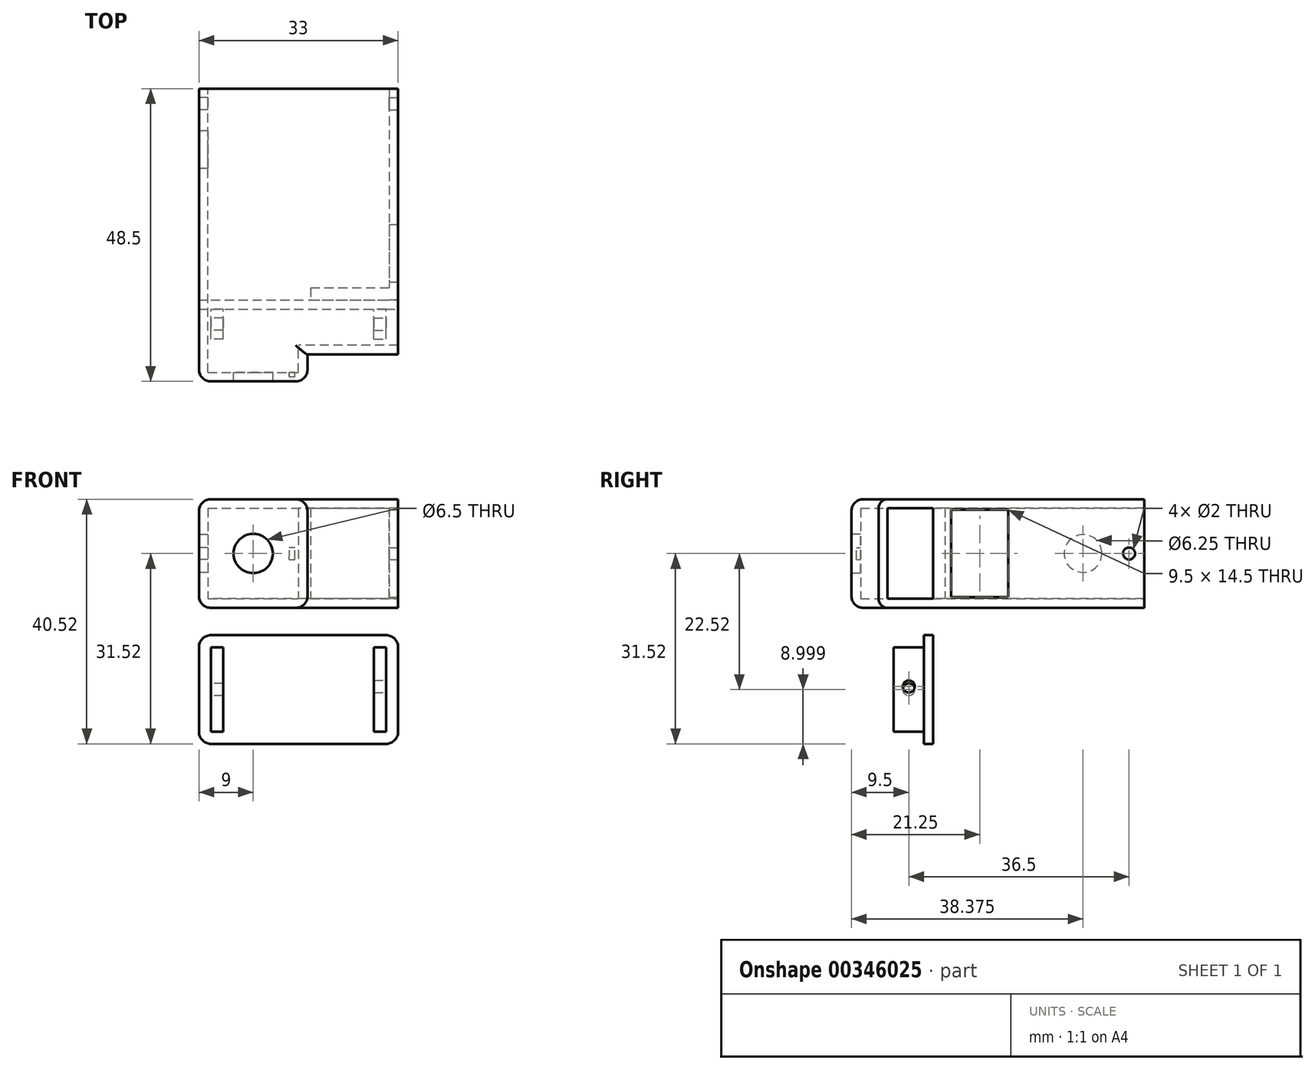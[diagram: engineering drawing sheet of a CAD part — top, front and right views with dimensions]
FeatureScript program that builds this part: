
annotation { "Feature Type Name" : "Feature", "Feature Type Description" : "" }
export const myFeature = defineFeature(function(context is Context, id is Id, definition is map)
    precondition{}
    {
        {
            var Q0;
            Q0=qCreatedBy(makeId("Front.planeOp"),FACE);
            var sketch = newSketch(context, id + "F0", { "sketchPlane" : qUnion([Q0])});
            skCircle(sketch, "E0", {"center": v(7.5, 7) * mm, "radius": 4.5 * mm});
            skCircle(sketch, "E1", {"center": v(7.5, 7) * mm, "radius": 3.25 * mm});
            skCircle(sketch, "E2", {"center": v(7.5, 7) * mm, "radius": 1.5 * mm});
            skLineSegment(sketch, "E3", {"start": v(36.83, 0) * mm, "end": v(36.83, 9.5) * mm, "construction": true});
            skLineSegment(sketch, "E4", {"start": v(36.83, 9.5) * mm, "end": v(49.83, 9.5) * mm, "construction": true});
            skLineSegment(sketch, "E5", {"start": v(49.83, 9.5) * mm, "end": v(49.83, 0) * mm, "construction": true});
            skLineSegment(sketch, "E6", {"start": v(49.83, 0) * mm, "end": v(36.83, 0) * mm, "construction": true});
            skLineSegment(sketch, "E7.0", {"start": v(14, 7) * mm, "end": v(1, 7) * mm, "construction": true});
            skLineSegment(sketch, "E8", {"start": v(14, 7) * mm, "end": v(33.97, 7) * mm, "construction": true});
            skLineSegment(sketch, "E9.0", {"start": v(14, -2) * mm, "end": v(33.97, -2) * mm, "construction": true});
            skLineSegment(sketch, "E10.0", {"start": v(14, -2) * mm, "end": v(0, -2) * mm, "construction": true});
            skLineSegment(sketch, "E11.0", {"start": v(7.5, 16) * mm, "end": v(7.5, -2) * mm, "construction": true});
            skLineSegment(sketch, "E12.0", {"start": v(16.5, 16) * mm, "end": v(16.5, -2) * mm});
            skLineSegment(sketch, "E13", {"start": v(0, 14.5) * mm, "end": v(0, -0.5) * mm});
            skLineSegment(sketch, "E14", {"start": v(-1.5, 16) * mm, "end": v(-1.5, -2) * mm});
            skLineSegment(sketch, "E15", {"start": v(-1.5, -2) * mm, "end": v(16.5, -2) * mm});
            skLineSegment(sketch, "E16", {"start": v(15, 14.5) * mm, "end": v(15, -0.5) * mm});
            skLineSegment(sketch, "E17", {"start": v(0, -0.5) * mm, "end": v(32.99, -0.5) * mm, "construction": true});
            skLineSegment(sketch, "E18", {"start": v(0, -0.5) * mm, "end": v(15, -0.5) * mm});
            skLineSegment(sketch, "E19", {"start": v(0, 14.5) * mm, "end": v(33.86, 14.5) * mm, "construction": true});
            skLineSegment(sketch, "E20", {"start": v(-1.5, 16) * mm, "end": v(36.08, 16) * mm, "construction": true});
            skLineSegment(sketch, "E21", {"start": v(-1.5, 16) * mm, "end": v(16.5, 16) * mm});
            skLineSegment(sketch, "E22", {"start": v(0, 14.5) * mm, "end": v(15, 14.5) * mm});
            skLineSegment(sketch, "E23", {"start": v(16.5, 14.5) * mm, "end": v(31.5, 14.5) * mm});
            skLineSegment(sketch, "E24", {"start": v(31.5, 14.5) * mm, "end": v(31.5, -0.5) * mm});
            skLineSegment(sketch, "E25", {"start": v(31.5, -0.5) * mm, "end": v(16.5, -0.5) * mm});
            skLineSegment(sketch, "E26", {"start": v(16.5, 16) * mm, "end": v(34.5, 16) * mm});
            skLineSegment(sketch, "E27", {"start": v(34.5, -2) * mm, "end": v(16.5, -2) * mm});
            skLineSegment(sketch, "E28.0", {"start": v(33, 16) * mm, "end": v(33, -2) * mm, "construction": true});
            skLineSegment(sketch, "E29", {"start": v(33, 16) * mm, "end": v(33, -2) * mm});
            skLineSegment(sketch, "E30", {"start": v(16.5, 14.5) * mm, "end": v(16.5, -0.5) * mm});
            skCircle(sketch, "E31", {"center": v(7.5, 7) * mm, "radius": 6 * mm});
            skSolve(sketch);
        }
        {
            var Q0;
            Q0=makeQuery(id+"F0.imprint","IMPRINT",FACE,{"disambiguationData":[TD([[makeQuery(id+"F0.imprint","IMPRINT",EDGE,{"derivedFrom":sQuery(id+"F0.wireOp",EDGE,"LJwKmjQE-U71p-W845-ssy2-OsRAPNaDEyHZ")}),1.0]])]});
            var Q1;
            Q1=makeQuery(id+"F0.imprint","IMPRINT",FACE,{"disambiguationData":[TD([[makeQuery(id+"F0.imprint","IMPRINT",EDGE,{"derivedFrom":sQuery(id+"F0.wireOp",EDGE,"E13")}),-1.0]])]});
            extrude(context, id + "F1", {"entities" : qUnion([Q0, Q1]), "depth" : 13.5 * mm});
        }
        {
            var Q0;
            Q0=makeQuery(id+"F0.imprint","IMPRINT",FACE,{"disambiguationData":[TD([[makeQuery(id+"F0.imprint","IMPRINT",EDGE,{"derivedFrom":sQuery(id+"F0.wireOp",EDGE,"E13")}),1.0]])]});
            extrude(context, id + "F2", {"entities" : qUnion([Q0]), "depth" : 13.5 * mm});
        }
        {
            var Q0;
            Q0=makeQuery(id+"F0.imprint","IMPRINT",FACE,{"disambiguationData":[TD([[makeQuery(id+"F0.imprint","IMPRINT",EDGE,{"derivedFrom":sQuery(id+"F0.wireOp",EDGE,"E13")}),1.0]])]});
            var Q1;
            Q1=makeQuery(id+"F0.imprint","IMPRINT",FACE,{"disambiguationData":[TD([[makeQuery(id+"F0.imprint","IMPRINT",EDGE,{"derivedFrom":sQuery(id+"F0.wireOp",EDGE,"E0")}),-1.0]])]});
            extrude(context, id + "F3", {"entities" : qUnion([Q0, Q1]), "operationType" : NewBodyOperationType.REMOVE, "depth" : 12 * mm});
        }
        {
            var Q0;
            Q0=makeQuery(id+"F1.opExtrude","SWEPT_FACE",FACE,{"disambiguationData":[OSD([sQuery(id+"F0.wireOp",EDGE,"E12.0"),sQuery(id+"F0.wireOp",EDGE,"E30")])]});
            var sketch = newSketch(context, id + "F4", { "sketchPlane" : qUnion([Q0])});
            skLineSegment(sketch, "E32.0", {"start": v(-13.5, 7) * mm, "end": v(0, 7) * mm, "construction": true});
            skLineSegment(sketch, "E33.0", {"start": v(-7.5, 16) * mm, "end": v(-7.5, -2) * mm, "construction": true});
            skLineSegment(sketch, "E34.0", {"start": v(-9, 16) * mm, "end": v(-9, -2) * mm, "construction": true});
            skLineSegment(sketch, "E35.0", {"start": v(-13.5, -0.5) * mm, "end": v(0, -0.5) * mm, "construction": true});
            skLineSegment(sketch, "E36.0", {"start": v(-13.5, 14.5) * mm, "end": v(0, 14.5) * mm, "construction": true});
            skLineSegment(sketch, "E37", {"start": v(0, -0.5) * mm, "end": v(-7.5, -0.5) * mm});
            skLineSegment(sketch, "E38", {"start": v(-7.5, -0.5) * mm, "end": v(-7.5, 14.5) * mm});
            skLineSegment(sketch, "E39", {"start": v(-7.5, 14.5) * mm, "end": v(0, 14.5) * mm});
            skLineSegment(sketch, "E40", {"start": v(0, -2) * mm, "end": v(-9, -2) * mm});
            skLineSegment(sketch, "E41", {"start": v(-9, 16) * mm, "end": v(0, 16) * mm});
            skLineSegment(sketch, "E42", {"start": v(-9, -2) * mm, "end": v(-9, 16) * mm});
            skSolve(sketch);
        }
        {
            var Q0;
            {var subQ2=sQuery(id+"F4.wireOp",EDGE,"E37");Q0=makeQuery(id+"F4.imprint","IMPRINT",FACE,{"disambiguationData":[TD([[makeQuery(id+"F4.imprint","IMPRINT",EDGE,{"derivedFrom":subQ2}),1.0]])]});}
            extrude(context, id + "F5", {"entities" : qUnion([Q0]), "operationType" : NewBodyOperationType.ADD, "depth" : 15 * mm});
        }
        {
            var Q0;
            {var subQ0=sQuery(id+"F4.wireOp",EDGE,"E37");var subQ1=sQuery(id+"F0.wireOp",EDGE,"E30");var subQ2=sQuery(id+"F0.wireOp",EDGE,"E12.0");Q0=makeQuery(id+"F5.boolean.opBoolean","SPLIT",FACE,{"disambiguationData":[TD([makeQuery(id+"F5.opExtrude","SWEPT_FACE",FACE,{"disambiguationData":[OSD([subQ0])]})])],"derivedFrom":makeQuery(id+"F1.opExtrude","SWEPT_FACE",FACE,{"disambiguationData":[OSD([subQ2,subQ1])]})});}
            extrude(context, id + "F6", {"entities" : qUnion([Q0]), "operationType" : NewBodyOperationType.REMOVE, "oppositeDirection" : true, "depth" : 1.5 * mm});
        }
        {
            var Q0;
            Q0=makeQuery(id+"F0.imprint","IMPRINT",FACE,{"disambiguationData":[TD([[makeQuery(id+"F0.imprint","IMPRINT",EDGE,{"derivedFrom":sQuery(id+"F0.wireOp",EDGE,"E13")}),-1.0]])]});
            var Q1;
            {var subQ0=sQuery(id+"F0.wireOp",EDGE,"E23");Q1=makeQuery(id+"F0.imprint","IMPRINT",FACE,{"disambiguationData":[TD([[makeQuery(id+"F0.imprint","IMPRINT",EDGE,{"derivedFrom":subQ0}),1.0]])]});}
            extrude(context, id + "F7", {"entities" : qUnion([Q0, Q1]), "operationType" : NewBodyOperationType.ADD, "oppositeDirection" : true, "depth" : 35 * mm});
        }
        {
            var Q0;
            Q0=makeQuery(id+"F7.opExtrude","CAP_FACE",FACE,{"disambiguationData":[OSD([sQuery(id+"F0.wireOp",EDGE,"E13"),sQuery(id+"F0.wireOp",EDGE,"E14"),sQuery(id+"F0.wireOp",EDGE,"E15"),sQuery(id+"F0.wireOp",EDGE,"E16"),sQuery(id+"F0.wireOp",EDGE,"E18"),sQuery(id+"F0.wireOp",EDGE,"E21"),sQuery(id+"F0.wireOp",EDGE,"E22"),sQuery(id+"F0.wireOp",EDGE,"E23"),sQuery(id+"F0.wireOp",EDGE,"E24"),sQuery(id+"F0.wireOp",EDGE,"E25"),sQuery(id+"F0.wireOp",EDGE,"E26"),sQuery(id+"F0.wireOp",EDGE,"E27"),sQuery(id+"F0.wireOp",EDGE,"E29"),sQuery(id+"F0.wireOp",EDGE,"E30")])],"isStart":false});
            var sketch = newSketch(context, id + "F8", { "sketchPlane" : qUnion([Q0])});
            skLineSegment(sketch, "E43", {"start": v(-16.5, 14.5) * mm, "end": v(-15, 14.5) * mm});
            skLineSegment(sketch, "E44", {"start": v(-15, 14.5) * mm, "end": v(-15, -0.5) * mm});
            skLineSegment(sketch, "E45", {"start": v(-15, -0.5) * mm, "end": v(-16.5, -0.5) * mm});
            skSolve(sketch);
        }
        {
            var Q0;
            Q0=makeQuery(id+"F8.imprint","IMPRINT",FACE,{"disambiguationData":[TD([[makeQuery(id+"F8.imprint","IMPRINT",EDGE,{"derivedFrom":sQuery(id+"F8.wireOp",EDGE,"E43")}),-1.0]])]});
            extrude(context, id + "F9", {"entities" : qUnion([Q0]), "operationType" : NewBodyOperationType.REMOVE, "oppositeDirection" : true, "depth" : 15 * mm});
        }
        {
            var Q0;
            Q0=makeQuery(id+"F7.opExtrude","SWEPT_FACE",FACE,{"disambiguationData":[OSD([sQuery(id+"F0.wireOp",EDGE,"E24")])]});
            var sketch = newSketch(context, id + "F10", { "sketchPlane" : qUnion([Q0])});
            skLineSegment(sketch, "E46.0", {"start": v(-15, 7) * mm, "end": v(0, 7) * mm, "construction": true});
            skLineSegment(sketch, "E47.0", {"start": v(-2, 14.5) * mm, "end": v(-2, -0.5) * mm, "construction": true});
            skLineSegment(sketch, "E48", {"start": v(-2, 14.5) * mm, "end": v(-2, -0.5) * mm});
            skSolve(sketch);
        }
        {
            var Q0;
            {var subQ0=sQuery(id+"F10.wireOp",EDGE,"E48");Q0=makeQuery(id+"F10.imprint","IMPRINT",FACE,{"disambiguationData":[TD([[makeQuery(id+"F10.imprint","IMPRINT",EDGE,{"derivedFrom":subQ0}),1.0]])]});}
            extrude(context, id + "F11", {"entities" : qUnion([Q0]), "operationType" : NewBodyOperationType.ADD, "depth" : 15 * mm});
        }
        {
            var Q0;
            Q0=makeQuery(id+"F7.opExtrude","CAP_FACE",FACE,{"disambiguationData":[OSD([sQuery(id+"F0.wireOp",EDGE,"E13"),sQuery(id+"F0.wireOp",EDGE,"E14"),sQuery(id+"F0.wireOp",EDGE,"E15"),sQuery(id+"F0.wireOp",EDGE,"E16"),sQuery(id+"F0.wireOp",EDGE,"E18"),sQuery(id+"F0.wireOp",EDGE,"E21"),sQuery(id+"F0.wireOp",EDGE,"E22"),sQuery(id+"F0.wireOp",EDGE,"E23"),sQuery(id+"F0.wireOp",EDGE,"E24"),sQuery(id+"F0.wireOp",EDGE,"E25"),sQuery(id+"F0.wireOp",EDGE,"E26"),sQuery(id+"F0.wireOp",EDGE,"E27"),sQuery(id+"F0.wireOp",EDGE,"E29"),sQuery(id+"F0.wireOp",EDGE,"E30")])],"isStart":false});
            var sketch = newSketch(context, id + "F12", { "sketchPlane" : qUnion([Q0])});
            skLineSegment(sketch, "E49", {"start": v(-31.5, -0.5) * mm, "end": v(-31.5, -2) * mm});
            skLineSegment(sketch, "E50", {"start": v(-31.5, 14.5) * mm, "end": v(-31.5, 16) * mm});
            skSolve(sketch);
        }
        {
            var Q0;
            {var subQ2=sQuery(id+"F12.wireOp",EDGE,"E49");Q0=makeQuery(id+"F12.imprint","IMPRINT",FACE,{"disambiguationData":[TD([[makeQuery(id+"F12.imprint","IMPRINT",EDGE,{"derivedFrom":subQ2}),-1.0]])]});}
            extrude(context, id + "F13", {"entities" : qUnion([Q0]), "operationType" : NewBodyOperationType.REMOVE, "oppositeDirection" : true, "depth" : 35 * mm});
        }
        {
            var Q0;
            Q0=makeQuery(id+"F11.opExtrude","SWEPT_FACE",FACE,{"disambiguationData":[OSD([sQuery(id+"F10.wireOp",EDGE,"E48")])]});
            var sketch = newSketch(context, id + "F14", { "sketchPlane" : qUnion([Q0])});
            skLineSegment(sketch, "E51.0", {"start": v(-30, 14.5) * mm, "end": v(-30, -0.5) * mm});
            skSolve(sketch);
        }
        {
            var Q0;
            {var subQ0=sQuery(id+"F14.wireOp",EDGE,"E51.0");Q0=makeQuery(id+"F14.imprint","IMPRINT",FACE,{"disambiguationData":[TD([[makeQuery(id+"F14.imprint","IMPRINT",EDGE,{"derivedFrom":subQ0}),-1.0]])]});}
            extrude(context, id + "F15", {"entities" : qUnion([Q0]), "operationType" : NewBodyOperationType.ADD, "depth" : 33 * mm});
        }
        {
            var Q0;
            Q0=qCreatedBy(makeId("Front.planeOp"),FACE);
            var sketch = newSketch(context, id + "F16", { "sketchPlane" : qUnion([Q0])});
            skLineSegment(sketch, "E52.0", {"start": v(-1.5, -6.52) * mm, "end": v(31.5, -6.52) * mm});
            skLineSegment(sketch, "E52.1", {"start": v(-1.5, -24.52) * mm, "end": v(-1.5, -6.52) * mm});
            skLineSegment(sketch, "E52.2", {"start": v(31.5, -24.52) * mm, "end": v(-1.5, -24.52) * mm});
            skLineSegment(sketch, "E52.3", {"start": v(31.5, -6.52) * mm, "end": v(31.5, -24.52) * mm});
            skLineSegment(sketch, "E53.0", {"start": v(0.5, -23.02) * mm, "end": v(0.5, -8.02) * mm});
            skLineSegment(sketch, "E54", {"start": v(29.5, -23.02) * mm, "end": v(29.5, -8.02) * mm});
            skLineSegment(sketch, "E55.0", {"start": v(30, -23.02) * mm, "end": v(30, -8.02) * mm});
            skLineSegment(sketch, "E56.0", {"start": v(0, -23.02) * mm, "end": v(0, -8.02) * mm});
            skLineSegment(sketch, "E57", {"start": v(0, -23.02) * mm, "end": v(30, -23.02) * mm});
            skLineSegment(sketch, "E58", {"start": v(0, -8.02) * mm, "end": v(30, -8.02) * mm});
            skLineSegment(sketch, "E59.0", {"start": v(0.5, -15.52) * mm, "end": v(29.5, -15.52) * mm, "construction": true});
            skLineSegment(sketch, "E60.0", {"start": v(0.5, -22.52) * mm, "end": v(29.5, -22.52) * mm, "construction": true});
            skLineSegment(sketch, "E61.0", {"start": v(0.5, -8.52) * mm, "end": v(29.5, -8.52) * mm, "construction": true});
            skLineSegment(sketch, "E62.0", {"start": v(2.5, -23.02) * mm, "end": v(2.5, -8.02) * mm, "construction": true});
            skLineSegment(sketch, "E63", {"start": v(2.5, -8.52) * mm, "end": v(2.5, -22.52) * mm});
            skLineSegment(sketch, "E64", {"start": v(2.5, -22.52) * mm, "end": v(0.5, -22.52) * mm});
            skLineSegment(sketch, "E65", {"start": v(2.5, -8.52) * mm, "end": v(0.5, -8.52) * mm});
            skLineSegment(sketch, "E66.0", {"start": v(27.5, -23.02) * mm, "end": v(27.5, -8.02) * mm, "construction": true});
            skLineSegment(sketch, "E67", {"start": v(29.5, -8.52) * mm, "end": v(27.5, -8.52) * mm});
            skLineSegment(sketch, "E68", {"start": v(27.5, -8.52) * mm, "end": v(27.5, -22.52) * mm});
            skLineSegment(sketch, "E69", {"start": v(27.5, -22.52) * mm, "end": v(29.5, -22.52) * mm});
            skSolve(sketch);
        }
        {
            var Q0;
            {var subQ0=sQuery(id+"F16.wireOp",EDGE,"c1f00315-3677-4781-b9ec-f24341b2bddf.0");Q0=makeQuery(id+"F16.imprint","IMPRINT",FACE,{"disambiguationData":[TD([[makeQuery(id+"F16.imprint","IMPRINT",EDGE,{"derivedFrom":subQ0}),-1.0]])]});}
            var Q1;
            {var subQ6=sQuery(id+"F16.wireOp",EDGE,"Nllkzhj5-O9xc-pzLj-AnTb-SjLHvJoBE1x8");Q1=makeQuery(id+"F16.imprint","IMPRINT",FACE,{"disambiguationData":[TD([[makeQuery(id+"F16.imprint","IMPRINT",EDGE,{"derivedFrom":subQ6}),1.0]])]});}
            var Q2;
            Q2=makeQuery(id+"F16.imprint","IMPRINT",FACE,{"disambiguationData":[TD([[makeQuery(id+"F16.imprint","IMPRINT",EDGE,{"derivedFrom":sQuery(id+"F16.wireOp",EDGE,"E52.0")}),-1.0]])]});
            var Q3;
            {var subQ5=sQuery(id+"F16.wireOp",EDGE,"E53.0");var subQ7=sQuery(id+"F16.wireOp",EDGE,"E57");var subQ8=makeQuery(id+"F16.imprint","INTERSECT",VERTEX,{"derivedFrom":[subQ5,subQ7]});Q3=makeQuery(id+"F16.imprint","IMPRINT",FACE,{"disambiguationData":[TD([[makeQuery(id+"F16.imprint","IMPRINT",EDGE,{"disambiguationData":[TD([[subQ8,-1.0]])],"derivedFrom":subQ5}),-1.0]])]});}
            var Q4;
            {var subQ0=sQuery(id+"F16.wireOp",EDGE,"cuP8Dtkg-PeRc-ziYg-5Cu8-oMthaOjJiXqI");Q4=makeQuery(id+"F16.imprint","IMPRINT",FACE,{"disambiguationData":[TD([[makeQuery(id+"F16.imprint","IMPRINT",EDGE,{"derivedFrom":subQ0}),-1.0]])]});}
            var Q5;
            {var subQ4=sQuery(id+"F16.wireOp",EDGE,"E53.0");var subQ7=sQuery(id+"F16.wireOp",EDGE,"E58");var subQ8=makeQuery(id+"F16.imprint","INTERSECT",VERTEX,{"derivedFrom":[subQ4,subQ7]});Q5=makeQuery(id+"F16.imprint","IMPRINT",FACE,{"disambiguationData":[TD([[makeQuery(id+"F16.imprint","IMPRINT",EDGE,{"disambiguationData":[TD([[subQ8,1.0]])],"derivedFrom":subQ4}),-1.0]])]});}
            var Q6;
            {var subQ0=sQuery(id+"F16.wireOp",EDGE,"E55.0");Q6=makeQuery(id+"F16.imprint","IMPRINT",FACE,{"disambiguationData":[TD([[makeQuery(id+"F16.imprint","IMPRINT",EDGE,{"derivedFrom":subQ0}),1.0]])]});}
            var Q7;
            {var subQ5=sQuery(id+"F16.wireOp",EDGE,"E56.0");Q7=makeQuery(id+"F16.imprint","IMPRINT",FACE,{"disambiguationData":[TD([[makeQuery(id+"F16.imprint","IMPRINT",EDGE,{"derivedFrom":subQ5}),-1.0]])]});}
            extrude(context, id + "F17", {"entities" : qUnion([Q0, Q1, Q2, Q3, Q4, Q5, Q6, Q7]), "depth" : 1.5 * mm});
        }
        {
            var Q0;
            {var subQ0=sQuery(id+"F16.wireOp",EDGE,"OV1JdslM-Z20a-Eb3S-tFHv-mYLRDY6jLDuE");Q0=makeQuery(id+"F16.imprint","IMPRINT",FACE,{"disambiguationData":[TD([[makeQuery(id+"F16.imprint","IMPRINT",EDGE,{"derivedFrom":subQ0}),-1.0]])]});}
            var Q1;
            {var subQ0=sQuery(id+"F16.wireOp",EDGE,"Nllkzhj5-O9xc-pzLj-AnTb-SjLHvJoBE1x8");Q1=makeQuery(id+"F16.imprint","IMPRINT",FACE,{"disambiguationData":[TD([[makeQuery(id+"F16.imprint","IMPRINT",EDGE,{"derivedFrom":subQ0}),-1.0]])]});}
            var Q2;
            {var subQ3=sQuery(id+"F16.wireOp",EDGE,"cuP8Dtkg-PeRc-ziYg-5Cu8-oMthaOjJiXqI");Q2=makeQuery(id+"F16.imprint","IMPRINT",FACE,{"disambiguationData":[TD([[makeQuery(id+"F16.imprint","IMPRINT",EDGE,{"derivedFrom":subQ3}),1.0]])]});}
            var Q3;
            {var subQ5=sQuery(id+"F16.wireOp",EDGE,"igbmhv8O-FM8D-jvqr-zpBT-GjGQ7EsZjF5f");Q3=makeQuery(id+"F16.imprint","IMPRINT",FACE,{"disambiguationData":[TD([[makeQuery(id+"F16.imprint","IMPRINT",EDGE,{"derivedFrom":subQ5}),1.0]])]});}
            var Q4;
            Q4=makeQuery(id+"F16.imprint","IMPRINT",FACE,{"disambiguationData":[TD([[makeQuery(id+"F16.imprint","IMPRINT",EDGE,{"derivedFrom":sQuery(id+"F16.wireOp",EDGE,"E63")}),-1.0]])]});
            var Q5;
            {var subQ0=sQuery(id+"F16.wireOp",EDGE,"E67");Q5=makeQuery(id+"F16.imprint","IMPRINT",FACE,{"disambiguationData":[TD([[makeQuery(id+"F16.imprint","IMPRINT",EDGE,{"derivedFrom":subQ0}),1.0]])]});}
            extrude(context, id + "F18", {"entities" : qUnion([Q0, Q1, Q2, Q3, Q4, Q5]), "operationType" : NewBodyOperationType.ADD, "depth" : 6.5 * mm});
        }
        {
            var Q0;
            Q0=makeQuery(id+"F18.opExtrude","SWEPT_FACE",FACE,{"disambiguationData":[OSD([sQuery(id+"F16.wireOp",EDGE,"E54")])]});
            var sketch = newSketch(context, id + "F19", { "sketchPlane" : qUnion([Q0])});
            skLineSegment(sketch, "E70.0", {"start": v(3.5, -15.02) * mm, "end": v(-11.5, -15.02) * mm, "construction": true});
            skLineSegment(sketch, "E71.0", {"start": v(-4, -22.02) * mm, "end": v(-4, -9.02) * mm, "construction": true});
            skCircle(sketch, "E72", {"center": v(-4, -15.02) * mm, "radius": 1 * mm});
            skSolve(sketch);
        }
        {
            var Q0;
            {var subQ0=sQuery(id+"F0.wireOp",EDGE,"E14");Q0=makeQuery(id+"F7.boolean.opBoolean","MERGE",FACE,{"derivedFrom":[makeQuery(id+"F1.opExtrude","SWEPT_FACE",FACE,{"disambiguationData":[OSD([subQ0])]}),makeQuery(id+"F7.opExtrude","SWEPT_FACE",FACE,{"disambiguationData":[OSD([subQ0])]})]});}
            var sketch = newSketch(context, id + "F20", { "sketchPlane" : qUnion([Q0])});
            skLineSegment(sketch, "E73.0", {"start": v(-32.5, 16) * mm, "end": v(-32.5, -2) * mm, "construction": true});
            skLineSegment(sketch, "E74.0", {"start": v(13.5, 7) * mm, "end": v(-15, 7) * mm, "construction": true});
            skCircle(sketch, "E75", {"center": v(-32.5, 7) * mm, "radius": 1 * mm});
            skLineSegment(sketch, "E76.0", {"start": v(-30, 16) * mm, "end": v(-30, -2) * mm, "construction": true});
            skLineSegment(sketch, "E77.0", {"start": v(-24.88, 16) * mm, "end": v(-24.88, -2) * mm, "construction": true});
            skLineSegment(sketch, "E78", {"start": v(-24.88, 7) * mm, "end": v(-24.88, 13.5) * mm, "construction": true});
            skCircle(sketch, "E79", {"center": v(-24.88, 7) * mm, "radius": 3.12 * mm});
            skSolve(sketch);
        }
        {
            var Q0;
            Q0=makeQuery(id+"F20.imprint","IMPRINT",FACE,{"disambiguationData":[TD([[makeQuery(id+"F20.imprint","IMPRINT",EDGE,{"derivedFrom":sQuery(id+"F20.wireOp",EDGE,"E75")}),1.0]])]});
            var Q1;
            Q1=sQuery(id+"F20.wireOp",EDGE,"E75");
            extrude(context, id + "F21", {"entities" : qUnion([Q0]), "operationType" : NewBodyOperationType.REMOVE, "surfaceEntities" : qUnion([Q1]), "oppositeDirection" : true, "depth" : 1.5 * mm});
        }
        {
            var Q0;
            Q0=makeQuery(id+"F15.boolean.opBoolean","MERGE",FACE,{"derivedFrom":[makeQuery(id+"F13.boolean.opBoolean","MERGE",FACE,{"derivedFrom":[makeQuery(id+"F5.opExtrude","CAP_FACE",FACE,{"disambiguationData":[OSD([sQuery(id+"F0.wireOp",EDGE,"E12.0"),sQuery(id+"F0.wireOp",EDGE,"E30"),sQuery(id+"F4.wireOp",EDGE,"E37"),sQuery(id+"F4.wireOp",EDGE,"E38"),sQuery(id+"F4.wireOp",EDGE,"E39"),sQuery(id+"F4.wireOp",EDGE,"E40"),sQuery(id+"F4.wireOp",EDGE,"E41"),sQuery(id+"F4.wireOp",EDGE,"E42")])],"isStart":false}),makeQuery(id+"F13.opExtrude","SWEPT_FACE",FACE,{"disambiguationData":[OSD([sQuery(id+"F0.wireOp",EDGE,"E24"),sQuery(id+"F12.wireOp",EDGE,"E49"),sQuery(id+"F12.wireOp",EDGE,"E50")])]})]}),makeQuery(id+"F15.opExtrude","SWEPT_FACE",FACE,{"disambiguationData":[OSD([sQuery(id+"F10.wireOp",EDGE,"E48")])]})]});
            var sketch = newSketch(context, id + "F22", { "sketchPlane" : qUnion([Q0])});
            skLineSegment(sketch, "E80.0", {"start": v(32.5, 16) * mm, "end": v(32.5, -2) * mm, "construction": true});
            skLineSegment(sketch, "E81.0", {"start": v(-9, 7) * mm, "end": v(15, 7) * mm, "construction": true});
            skCircle(sketch, "E82", {"center": v(32.5, 7) * mm, "radius": 1 * mm});
            skSolve(sketch);
        }
        {
            var Q0;
            Q0=makeQuery(id+"F22.imprint","IMPRINT",FACE,{"disambiguationData":[TD([[makeQuery(id+"F22.imprint","IMPRINT",EDGE,{"derivedFrom":sQuery(id+"F22.wireOp",EDGE,"E82")}),1.0]])]});
            var Q1;
            Q1=sQuery(id+"F22.wireOp",EDGE,"E82");
            extrude(context, id + "F23", {"entities" : qUnion([Q0]), "operationType" : NewBodyOperationType.REMOVE, "surfaceEntities" : qUnion([Q1]), "oppositeDirection" : true, "depth" : 1.5 * mm});
        }
        {
            var Q0;
            Q0=makeQuery(id+"F20.imprint","IMPRINT",FACE,{"disambiguationData":[TD([[makeQuery(id+"F20.imprint","IMPRINT",EDGE,{"derivedFrom":sQuery(id+"F20.wireOp",EDGE,"wNZCuEQn-TdIB-Z6ur-80ty-3GzjuUfzDEaF")}),-1.0]])]});
            var Q1;
            Q1=makeQuery(id+"F20.imprint","IMPRINT",FACE,{"disambiguationData":[TD([[makeQuery(id+"F20.imprint","IMPRINT",EDGE,{"derivedFrom":sQuery(id+"F20.wireOp",EDGE,"E79")}),1.0]])]});
            extrude(context, id + "F24", {"entities" : qUnion([Q0, Q1]), "operationType" : NewBodyOperationType.REMOVE, "oppositeDirection" : true, "depth" : 1.5 * mm});
        }
        {
            var Q0;
            Q0=makeQuery(id+"F3.boolean.opBoolean","COPY",FACE,{"derivedFrom":makeQuery(id+"F3.opExtrude","CAP_FACE",FACE,{"disambiguationData":[OSD([sQuery(id+"F0.wireOp",EDGE,"E0"),sQuery(id+"F0.wireOp",EDGE,"E13"),sQuery(id+"F0.wireOp",EDGE,"E16"),sQuery(id+"F0.wireOp",EDGE,"E18"),sQuery(id+"F0.wireOp",EDGE,"E22")])],"isStart":false})});
            var sketch = newSketch(context, id + "F25", { "sketchPlane" : qUnion([Q0])});
            skLineSegment(sketch, "E83.0", {"start": v(0, 7) * mm, "end": v(-15, 7) * mm, "construction": true});
            skLineSegment(sketch, "E84", {"start": v(-13.5, 7) * mm, "end": v(-13.5, 6) * mm, "construction": true});
            skLineSegment(sketch, "E85", {"start": v(-13.5, 7) * mm, "end": v(-13.5, 8) * mm, "construction": true});
            skLineSegment(sketch, "E86", {"start": v(-13.42, 6) * mm, "end": v(-14.42, 6) * mm});
            skLineSegment(sketch, "E87", {"start": v(-14.42, 6) * mm, "end": v(-14.42, 7) * mm});
            skLineSegment(sketch, "E88", {"start": v(-14.42, 7) * mm, "end": v(-14.42, 8) * mm});
            skLineSegment(sketch, "E89", {"start": v(-14.42, 8) * mm, "end": v(-13.42, 8) * mm});
            skSolve(sketch);
        }
        {
            var Q0;
            {var subQ1=sQuery(id+"F25.wireOp",EDGE,"E86");Q0=makeQuery(id+"F25.imprint","IMPRINT",FACE,{"disambiguationData":[TD([[makeQuery(id+"F25.imprint","IMPRINT",EDGE,{"derivedFrom":subQ1}),-1.0]])]});}
            extrude(context, id + "F26", {"entities" : qUnion([Q0]), "operationType" : NewBodyOperationType.REMOVE, "oppositeDirection" : true, "depth" : 0.7 * mm});
        }
        {
            var Q0;
            Q0=makeQuery(id+"F18.opExtrude","SWEPT_FACE",FACE,{"disambiguationData":[OSD([sQuery(id+"F16.wireOp",EDGE,"E53.0")])]});
            var sketch = newSketch(context, id + "F27", { "sketchPlane" : qUnion([Q0])});
            skLineSegment(sketch, "E90.0", {"start": v(6.5, -16.02) * mm, "end": v(11.5, -16.02) * mm, "construction": true});
            skLineSegment(sketch, "E91.0", {"start": v(4, -22.02) * mm, "end": v(4, -9.02) * mm, "construction": true});
            skCircle(sketch, "E92", {"center": v(4, -15.52) * mm, "radius": 1 * mm});
            skSolve(sketch);
        }
        {
            var Q0;
            Q0=makeQuery(id+"F27.imprint","IMPRINT",FACE,{"disambiguationData":[TD([[makeQuery(id+"F27.imprint","IMPRINT",EDGE,{"derivedFrom":sQuery(id+"F27.wireOp",EDGE,"E92")}),1.0]])]});
            extrude(context, id + "F28", {"entities" : qUnion([Q0]), "operationType" : NewBodyOperationType.REMOVE, "oppositeDirection" : true, "depth" : 2 * mm});
        }
        {
            var Q0;
            Q0=makeQuery(id+"F9.boolean.opBoolean","COPY",FACE,{"derivedFrom":makeQuery(id+"F9.opExtrude","CAP_FACE",FACE,{"disambiguationData":[OSD([sQuery(id+"F0.wireOp",EDGE,"E30"),sQuery(id+"F8.wireOp",EDGE,"E43"),sQuery(id+"F8.wireOp",EDGE,"E44"),sQuery(id+"F8.wireOp",EDGE,"E45")])],"isStart":false})});
            extrude(context, id + "F29", {"entities" : qUnion([Q0]), "operationType" : NewBodyOperationType.REMOVE, "oppositeDirection" : true, "depth" : 5 * mm});
        }
        {
            var Q0;
            Q0=makeQuery(id+"F7.opExtrude","SWEPT_FACE",FACE,{"disambiguationData":[OSD([sQuery(id+"F0.wireOp",EDGE,"E16")])]});
            extrude(context, id + "F30", {"entities" : qUnion([Q0]), "operationType" : NewBodyOperationType.REMOVE, "oppositeDirection" : true, "depth" : 2 * mm});
        }
        {
            var Q0;
            Q0=makeQuery(id+"F2.opExtrude","SWEPT_BODY",BODY,{"disambiguationData":[OSD([sQuery(id+"F0.wireOp",EDGE,"E13"),sQuery(id+"F0.wireOp",EDGE,"E16"),sQuery(id+"F0.wireOp",EDGE,"E18"),sQuery(id+"F0.wireOp",EDGE,"E22"),sQuery(id+"F0.wireOp",EDGE,"E31")])]});
            var Q1;
            Q1=makeQuery(id+"F1.opExtrude","SWEPT_BODY",BODY,{"disambiguationData":[OSD([sQuery(id+"F0.wireOp",EDGE,"E12.0"),sQuery(id+"F0.wireOp",EDGE,"E13"),sQuery(id+"F0.wireOp",EDGE,"E14"),sQuery(id+"F0.wireOp",EDGE,"E15"),sQuery(id+"F0.wireOp",EDGE,"E16"),sQuery(id+"F0.wireOp",EDGE,"E18"),sQuery(id+"F0.wireOp",EDGE,"E21"),sQuery(id+"F0.wireOp",EDGE,"E22"),sQuery(id+"F0.wireOp",EDGE,"E30")])]});
            booleanBodies(context, id + "F31", {"operationType" : BooleanOperationType.UNION, "tools" : qUnion([Q0, Q1])});
        }
        {
            var Q0;
            Q0=makeQuery(id+"F0.imprint","IMPRINT",FACE,{"disambiguationData":[TD([[makeQuery(id+"F0.imprint","IMPRINT",EDGE,{"derivedFrom":sQuery(id+"F0.wireOp",EDGE,"E0")}),-1.0]])]});
            extrude(context, id + "F32", {"entities" : qUnion([Q0]), "operationType" : NewBodyOperationType.ADD, "depth" : 13.5 * mm});
        }
        {
            var Q0;
            Q0=makeQuery(id+"F0.imprint","IMPRINT",FACE,{"disambiguationData":[TD([[makeQuery(id+"F0.imprint","IMPRINT",EDGE,{"derivedFrom":sQuery(id+"F0.wireOp",EDGE,"E0")}),-1.0]])]});
            extrude(context, id + "F33", {"entities" : qUnion([Q0]), "operationType" : NewBodyOperationType.REMOVE, "depth" : 12 * mm});
        }
        {
            var Q0;
            Q0=makeQuery(id+"F0.imprint","IMPRINT",FACE,{"disambiguationData":[TD([[makeQuery(id+"F0.imprint","IMPRINT",EDGE,{"derivedFrom":sQuery(id+"F0.wireOp",EDGE,"E0")}),1.0]])]});
            extrude(context, id + "F34", {"entities" : qUnion([Q0]), "operationType" : NewBodyOperationType.ADD, "depth" : 13.5 * mm});
        }
        {
            var Q0;
            Q0=makeQuery(id+"F0.imprint","IMPRINT",FACE,{"disambiguationData":[TD([[makeQuery(id+"F0.imprint","IMPRINT",EDGE,{"derivedFrom":sQuery(id+"F0.wireOp",EDGE,"E0")}),1.0]])]});
            extrude(context, id + "F35", {"entities" : qUnion([Q0]), "operationType" : NewBodyOperationType.REMOVE, "depth" : 12 * mm});
        }
        {
            var Q0;
            Q0=makeQuery(id+"F15.boolean.opBoolean","MERGE",FACE,{"derivedFrom":[makeQuery(id+"F13.boolean.opBoolean","MERGE",FACE,{"derivedFrom":[makeQuery(id+"F5.opExtrude","CAP_FACE",FACE,{"disambiguationData":[OSD([sQuery(id+"F0.wireOp",EDGE,"E12.0"),sQuery(id+"F0.wireOp",EDGE,"E30"),sQuery(id+"F4.wireOp",EDGE,"E37"),sQuery(id+"F4.wireOp",EDGE,"E38"),sQuery(id+"F4.wireOp",EDGE,"E39"),sQuery(id+"F4.wireOp",EDGE,"E40"),sQuery(id+"F4.wireOp",EDGE,"E41"),sQuery(id+"F4.wireOp",EDGE,"E42")])],"isStart":false}),makeQuery(id+"F13.opExtrude","SWEPT_FACE",FACE,{"disambiguationData":[OSD([sQuery(id+"F0.wireOp",EDGE,"E24"),sQuery(id+"F12.wireOp",EDGE,"E49"),sQuery(id+"F12.wireOp",EDGE,"E50")])]})]}),makeQuery(id+"F15.opExtrude","SWEPT_FACE",FACE,{"disambiguationData":[OSD([sQuery(id+"F10.wireOp",EDGE,"E48")])]})]});
            var sketch = newSketch(context, id + "F36", { "sketchPlane" : qUnion([Q0])});
            skLineSegment(sketch, "E93.0", {"start": v(-9, 7) * mm, "end": v(22, 7) * mm, "construction": true});
            skLineSegment(sketch, "E94.0", {"start": v(1.5, -0.5) * mm, "end": v(1.5, 14.5) * mm, "construction": true});
            skLineSegment(sketch, "E95", {"start": v(3, 7) * mm, "end": v(3, 14.25) * mm});
            skLineSegment(sketch, "E96", {"start": v(3, 14.25) * mm, "end": v(7.75, 14.25) * mm});
            skLineSegment(sketch, "E97.MirrorCS", {"start": v(3, 7) * mm, "end": v(3, -0.25) * mm});
            skLineSegment(sketch, "E98.MirrorCS", {"start": v(3, -0.25) * mm, "end": v(7.75, -0.25) * mm});
            skLineSegment(sketch, "E99", {"start": v(7.75, -0.25) * mm, "end": v(12.5, -0.25) * mm});
            skLineSegment(sketch, "E100", {"start": v(12.5, -0.25) * mm, "end": v(12.5, 7) * mm});
            skLineSegment(sketch, "E101", {"start": v(12.5, 7) * mm, "end": v(12.5, 14.25) * mm});
            skLineSegment(sketch, "E102", {"start": v(12.5, 14.25) * mm, "end": v(7.75, 14.25) * mm});
            skSolve(sketch);
        }
        {
            var Q0;
            Q0=makeQuery(id+"F36.imprint","IMPRINT",FACE,{"disambiguationData":[TD([[makeQuery(id+"F36.imprint","IMPRINT",EDGE,{"derivedFrom":sQuery(id+"F36.wireOp",EDGE,"E95")}),-1.0]])]});
            extrude(context, id + "F37", {"entities" : qUnion([Q0]), "operationType" : NewBodyOperationType.REMOVE, "oppositeDirection" : true, "depth" : 1.5 * mm});
        }
        {
            var Q0;
            Q0=makeQuery(id+"F15.opExtrude","CAP_EDGE",EDGE,{"disambiguationData":[OSD([sQuery(id+"F14.wireOp",EDGE,"E51.0")])],"isStart":true});
            var Q1;
            Q1=makeQuery(id+"F30.boolean.opBoolean","COPY",EDGE,{"derivedFrom":makeQuery(id+"F30.opExtrude","CAP_EDGE",EDGE,{"disambiguationData":[OSD([sQuery(id+"F8.wireOp",EDGE,"E44")])],"isStart":false})});
            var Q2;
            Q2=makeQuery(id+"F17.opExtrude","SWEPT_EDGE",EDGE,{"disambiguationData":[OSD([sQuery(id+"F16.wireOp",EDGE,"E52.2"),sQuery(id+"F16.wireOp",EDGE,"E52.3")])]});
            var Q3;
            Q3=makeQuery(id+"F17.opExtrude","SWEPT_EDGE",EDGE,{"disambiguationData":[OSD([sQuery(id+"F16.wireOp",EDGE,"E52.0"),sQuery(id+"F16.wireOp",EDGE,"E52.3")])]});
            var Q4;
            Q4=makeQuery(id+"F17.opExtrude","SWEPT_EDGE",EDGE,{"disambiguationData":[OSD([sQuery(id+"F16.wireOp",EDGE,"E52.0"),sQuery(id+"F16.wireOp",EDGE,"E52.1")])]});
            var Q5;
            Q5=makeQuery(id+"F17.opExtrude","SWEPT_EDGE",EDGE,{"disambiguationData":[OSD([sQuery(id+"F16.wireOp",EDGE,"E52.1"),sQuery(id+"F16.wireOp",EDGE,"E52.2")])]});
            fillet(context, id + "F38", {"entities" : qUnion([Q0, Q1, Q2, Q3, Q4, Q5]), "radius" : 2 * mm, "tangentPropagation" : true, "allowEdgeOverflow" : false});
        }
        {
            var Q0;
            Q0=makeQuery(id+"F13.boolean.opBoolean","MERGE",EDGE,{"derivedFrom":[makeQuery(id+"F5.opExtrude","CAP_EDGE",EDGE,{"disambiguationData":[OSD([sQuery(id+"F4.wireOp",EDGE,"E40")])],"isStart":false}),makeQuery(id+"F13.opExtrude","SWEPT_EDGE",EDGE,{"disambiguationData":[OSD([sQuery(id+"F0.wireOp",EDGE,"E15"),sQuery(id+"F0.wireOp",EDGE,"E27"),sQuery(id+"F12.wireOp",EDGE,"E49")])]})]});
            var Q1;
            Q1=makeQuery(id+"F13.boolean.opBoolean","MERGE",EDGE,{"derivedFrom":[makeQuery(id+"F5.opExtrude","CAP_EDGE",EDGE,{"disambiguationData":[OSD([sQuery(id+"F4.wireOp",EDGE,"E41")])],"isStart":false}),makeQuery(id+"F13.opExtrude","SWEPT_EDGE",EDGE,{"disambiguationData":[OSD([sQuery(id+"F0.wireOp",EDGE,"E21"),sQuery(id+"F0.wireOp",EDGE,"E26"),sQuery(id+"F12.wireOp",EDGE,"E50")])]})]});
            var Q2;
            {var subQ0=sQuery(id+"F0.wireOp",EDGE,"E21");var subQ1=sQuery(id+"F0.wireOp",EDGE,"E14");Q2=makeQuery(id+"F7.boolean.opBoolean","MERGE",EDGE,{"derivedFrom":[makeQuery(id+"F1.opExtrude","SWEPT_EDGE",EDGE,{"disambiguationData":[OSD([subQ1,subQ0])]}),makeQuery(id+"F7.opExtrude","SWEPT_EDGE",EDGE,{"disambiguationData":[OSD([subQ1,subQ0])]})]});}
            var Q3;
            {var subQ0=sQuery(id+"F0.wireOp",EDGE,"E15");var subQ1=sQuery(id+"F0.wireOp",EDGE,"E14");Q3=makeQuery(id+"F7.boolean.opBoolean","MERGE",EDGE,{"derivedFrom":[makeQuery(id+"F1.opExtrude","SWEPT_EDGE",EDGE,{"disambiguationData":[OSD([subQ1,subQ0])]}),makeQuery(id+"F7.opExtrude","SWEPT_EDGE",EDGE,{"disambiguationData":[OSD([subQ1,subQ0])]})]});}
            var Q4;
            Q4=makeQuery(id+"F1.opExtrude","SWEPT_EDGE",EDGE,{"disambiguationData":[OSD([sQuery(id+"F0.wireOp",EDGE,"E12.0"),sQuery(id+"F0.wireOp",EDGE,"E15"),sQuery(id+"F0.wireOp",EDGE,"E27")])]});
            var Q5;
            Q5=makeQuery(id+"F1.opExtrude","SWEPT_EDGE",EDGE,{"disambiguationData":[OSD([sQuery(id+"F0.wireOp",EDGE,"E12.0"),sQuery(id+"F0.wireOp",EDGE,"E21"),sQuery(id+"F0.wireOp",EDGE,"E26")])]});
            fillet(context, id + "F39", {"entities" : qUnion([Q0, Q1, Q2, Q3, Q4, Q5]), "radius" : 2 * mm, "tangentPropagation" : true, "allowEdgeOverflow" : false});
        }
        {
            var Q0;
            Q0=makeQuery(id+"F19.imprint","IMPRINT",FACE,{"disambiguationData":[TD([[makeQuery(id+"F19.imprint","IMPRINT",EDGE,{"derivedFrom":sQuery(id+"F19.wireOp",EDGE,"E72")}),1.0]])]});
            extrude(context, id + "F40", {"entities" : qUnion([Q0]), "operationType" : NewBodyOperationType.REMOVE, "oppositeDirection" : true, "depth" : 2 * mm});
        }
        {
            var Q0;
            Q0=makeQuery(id+"F1.opExtrude","CAP_EDGE",EDGE,{"disambiguationData":[OSD([sQuery(id+"F0.wireOp",EDGE,"E14")])],"isStart":false});
            var Q1;
            Q1=makeQuery(id+"F1.opExtrude","CAP_EDGE",EDGE,{"disambiguationData":[OSD([sQuery(id+"F0.wireOp",EDGE,"E21")])],"isStart":false});
            var Q2;
            Q2=makeQuery(id+"F1.opExtrude","CAP_EDGE",EDGE,{"disambiguationData":[OSD([sQuery(id+"F0.wireOp",EDGE,"E12.0"),sQuery(id+"F0.wireOp",EDGE,"E30")])],"isStart":false});
            var Q3;
            Q3=makeQuery(id+"F1.opExtrude","CAP_EDGE",EDGE,{"disambiguationData":[OSD([sQuery(id+"F0.wireOp",EDGE,"E15")])],"isStart":false});
            var Q4;
            {var subQ0=sQuery(id+"F0.wireOp",EDGE,"E0");var subQ1=sQuery(id+"F0.wireOp",EDGE,"E31");var subQ2=sQuery(id+"F0.wireOp",EDGE,"E22");var subQ3=sQuery(id+"F0.wireOp",EDGE,"E18");var subQ4=sQuery(id+"F0.wireOp",EDGE,"E16");var subQ5=sQuery(id+"F0.wireOp",EDGE,"E13");var subQ6=sQuery(id+"F0.wireOp",EDGE,"E15");var subQ7=sQuery(id+"F0.wireOp",EDGE,"E14");Q4=makeQuery(id+"F39.opFillet","BLEND_EDGE",EDGE,{"blendedFrom":[makeQuery(id+"F7.boolean.opBoolean","MERGE",EDGE,{"derivedFrom":[makeQuery(id+"F1.opExtrude","SWEPT_EDGE",EDGE,{"disambiguationData":[OSD([subQ7,subQ6])]}),makeQuery(id+"F7.opExtrude","SWEPT_EDGE",EDGE,{"disambiguationData":[OSD([subQ7,subQ6])]})]}),makeQuery(id+"F34.boolean.opBoolean","MERGE",FACE,{"derivedFrom":[makeQuery(id+"F32.boolean.opBoolean","MERGE",FACE,{"derivedFrom":[makeQuery(id+"F31.opBoolean","MERGE",FACE,{"derivedFrom":[makeQuery(id+"F1.opExtrude","CAP_FACE",FACE,{"disambiguationData":[OSD([sQuery(id+"F0.wireOp",EDGE,"E12.0"),subQ5,subQ7,subQ6,subQ4,subQ3,sQuery(id+"F0.wireOp",EDGE,"E21"),subQ2,sQuery(id+"F0.wireOp",EDGE,"E30")])],"isStart":false}),makeQuery(id+"F2.opExtrude","CAP_FACE",FACE,{"disambiguationData":[OSD([subQ5,subQ4,subQ3,subQ2,subQ1])],"isStart":false})]}),makeQuery(id+"F32.opExtrude","CAP_FACE",FACE,{"disambiguationData":[OSD([subQ0,subQ1])],"isStart":false})]}),makeQuery(id+"F34.opExtrude","CAP_FACE",FACE,{"disambiguationData":[OSD([subQ0,sQuery(id+"F0.wireOp",EDGE,"E1")])],"isStart":false})]})],"blendedInto":[makeQuery(id+"F34.boolean.opBoolean","MERGE",FACE,{"derivedFrom":[makeQuery(id+"F32.boolean.opBoolean","MERGE",FACE,{"derivedFrom":[makeQuery(id+"F31.opBoolean","MERGE",FACE,{"derivedFrom":[makeQuery(id+"F1.opExtrude","CAP_FACE",FACE,{"disambiguationData":[OSD([sQuery(id+"F0.wireOp",EDGE,"E12.0"),subQ5,subQ7,subQ6,subQ4,subQ3,sQuery(id+"F0.wireOp",EDGE,"E21"),subQ2,sQuery(id+"F0.wireOp",EDGE,"E30")])],"isStart":false}),makeQuery(id+"F2.opExtrude","CAP_FACE",FACE,{"disambiguationData":[OSD([subQ5,subQ4,subQ3,subQ2,subQ1])],"isStart":false})]}),makeQuery(id+"F32.opExtrude","CAP_FACE",FACE,{"disambiguationData":[OSD([subQ0,subQ1])],"isStart":false})]}),makeQuery(id+"F34.opExtrude","CAP_FACE",FACE,{"disambiguationData":[OSD([subQ0,sQuery(id+"F0.wireOp",EDGE,"E1")])],"isStart":false})]})]});}
            var Q5;
            {var subQ0=sQuery(id+"F0.wireOp",EDGE,"E0");var subQ1=sQuery(id+"F0.wireOp",EDGE,"E31");var subQ2=sQuery(id+"F0.wireOp",EDGE,"E22");var subQ3=sQuery(id+"F0.wireOp",EDGE,"E18");var subQ4=sQuery(id+"F0.wireOp",EDGE,"E16");var subQ5=sQuery(id+"F0.wireOp",EDGE,"E13");var subQ6=sQuery(id+"F0.wireOp",EDGE,"E21");var subQ7=sQuery(id+"F0.wireOp",EDGE,"E14");Q5=makeQuery(id+"F39.opFillet","BLEND_EDGE",EDGE,{"blendedFrom":[makeQuery(id+"F7.boolean.opBoolean","MERGE",EDGE,{"derivedFrom":[makeQuery(id+"F1.opExtrude","SWEPT_EDGE",EDGE,{"disambiguationData":[OSD([subQ7,subQ6])]}),makeQuery(id+"F7.opExtrude","SWEPT_EDGE",EDGE,{"disambiguationData":[OSD([subQ7,subQ6])]})]}),makeQuery(id+"F34.boolean.opBoolean","MERGE",FACE,{"derivedFrom":[makeQuery(id+"F32.boolean.opBoolean","MERGE",FACE,{"derivedFrom":[makeQuery(id+"F31.opBoolean","MERGE",FACE,{"derivedFrom":[makeQuery(id+"F1.opExtrude","CAP_FACE",FACE,{"disambiguationData":[OSD([sQuery(id+"F0.wireOp",EDGE,"E12.0"),subQ5,subQ7,sQuery(id+"F0.wireOp",EDGE,"E15"),subQ4,subQ3,subQ6,subQ2,sQuery(id+"F0.wireOp",EDGE,"E30")])],"isStart":false}),makeQuery(id+"F2.opExtrude","CAP_FACE",FACE,{"disambiguationData":[OSD([subQ5,subQ4,subQ3,subQ2,subQ1])],"isStart":false})]}),makeQuery(id+"F32.opExtrude","CAP_FACE",FACE,{"disambiguationData":[OSD([subQ0,subQ1])],"isStart":false})]}),makeQuery(id+"F34.opExtrude","CAP_FACE",FACE,{"disambiguationData":[OSD([subQ0,sQuery(id+"F0.wireOp",EDGE,"E1")])],"isStart":false})]})],"blendedInto":[makeQuery(id+"F34.boolean.opBoolean","MERGE",FACE,{"derivedFrom":[makeQuery(id+"F32.boolean.opBoolean","MERGE",FACE,{"derivedFrom":[makeQuery(id+"F31.opBoolean","MERGE",FACE,{"derivedFrom":[makeQuery(id+"F1.opExtrude","CAP_FACE",FACE,{"disambiguationData":[OSD([sQuery(id+"F0.wireOp",EDGE,"E12.0"),subQ5,subQ7,sQuery(id+"F0.wireOp",EDGE,"E15"),subQ4,subQ3,subQ6,subQ2,sQuery(id+"F0.wireOp",EDGE,"E30")])],"isStart":false}),makeQuery(id+"F2.opExtrude","CAP_FACE",FACE,{"disambiguationData":[OSD([subQ5,subQ4,subQ3,subQ2,subQ1])],"isStart":false})]}),makeQuery(id+"F32.opExtrude","CAP_FACE",FACE,{"disambiguationData":[OSD([subQ0,subQ1])],"isStart":false})]}),makeQuery(id+"F34.opExtrude","CAP_FACE",FACE,{"disambiguationData":[OSD([subQ0,sQuery(id+"F0.wireOp",EDGE,"E1")])],"isStart":false})]})]});}
            var Q6;
            {var subQ0=sQuery(id+"F0.wireOp",EDGE,"E0");var subQ1=sQuery(id+"F0.wireOp",EDGE,"E31");var subQ2=sQuery(id+"F0.wireOp",EDGE,"E22");var subQ3=sQuery(id+"F0.wireOp",EDGE,"E18");var subQ4=sQuery(id+"F0.wireOp",EDGE,"E16");var subQ5=sQuery(id+"F0.wireOp",EDGE,"E13");var subQ6=sQuery(id+"F0.wireOp",EDGE,"E21");var subQ7=sQuery(id+"F0.wireOp",EDGE,"E12.0");Q6=makeQuery(id+"F39.opFillet","BLEND_EDGE",EDGE,{"blendedFrom":[makeQuery(id+"F1.opExtrude","SWEPT_EDGE",EDGE,{"disambiguationData":[OSD([subQ7,subQ6,sQuery(id+"F0.wireOp",EDGE,"E26")])]}),makeQuery(id+"F34.boolean.opBoolean","MERGE",FACE,{"derivedFrom":[makeQuery(id+"F32.boolean.opBoolean","MERGE",FACE,{"derivedFrom":[makeQuery(id+"F31.opBoolean","MERGE",FACE,{"derivedFrom":[makeQuery(id+"F1.opExtrude","CAP_FACE",FACE,{"disambiguationData":[OSD([subQ7,subQ5,sQuery(id+"F0.wireOp",EDGE,"E14"),sQuery(id+"F0.wireOp",EDGE,"E15"),subQ4,subQ3,subQ6,subQ2,sQuery(id+"F0.wireOp",EDGE,"E30")])],"isStart":false}),makeQuery(id+"F2.opExtrude","CAP_FACE",FACE,{"disambiguationData":[OSD([subQ5,subQ4,subQ3,subQ2,subQ1])],"isStart":false})]}),makeQuery(id+"F32.opExtrude","CAP_FACE",FACE,{"disambiguationData":[OSD([subQ0,subQ1])],"isStart":false})]}),makeQuery(id+"F34.opExtrude","CAP_FACE",FACE,{"disambiguationData":[OSD([subQ0,sQuery(id+"F0.wireOp",EDGE,"E1")])],"isStart":false})]})],"blendedInto":[makeQuery(id+"F34.boolean.opBoolean","MERGE",FACE,{"derivedFrom":[makeQuery(id+"F32.boolean.opBoolean","MERGE",FACE,{"derivedFrom":[makeQuery(id+"F31.opBoolean","MERGE",FACE,{"derivedFrom":[makeQuery(id+"F1.opExtrude","CAP_FACE",FACE,{"disambiguationData":[OSD([subQ7,subQ5,sQuery(id+"F0.wireOp",EDGE,"E14"),sQuery(id+"F0.wireOp",EDGE,"E15"),subQ4,subQ3,subQ6,subQ2,sQuery(id+"F0.wireOp",EDGE,"E30")])],"isStart":false}),makeQuery(id+"F2.opExtrude","CAP_FACE",FACE,{"disambiguationData":[OSD([subQ5,subQ4,subQ3,subQ2,subQ1])],"isStart":false})]}),makeQuery(id+"F32.opExtrude","CAP_FACE",FACE,{"disambiguationData":[OSD([subQ0,subQ1])],"isStart":false})]}),makeQuery(id+"F34.opExtrude","CAP_FACE",FACE,{"disambiguationData":[OSD([subQ0,sQuery(id+"F0.wireOp",EDGE,"E1")])],"isStart":false})]})]});}
            var Q7;
            {var subQ0=sQuery(id+"F0.wireOp",EDGE,"E0");var subQ1=sQuery(id+"F0.wireOp",EDGE,"E31");var subQ2=sQuery(id+"F0.wireOp",EDGE,"E22");var subQ3=sQuery(id+"F0.wireOp",EDGE,"E18");var subQ4=sQuery(id+"F0.wireOp",EDGE,"E16");var subQ5=sQuery(id+"F0.wireOp",EDGE,"E13");var subQ6=sQuery(id+"F0.wireOp",EDGE,"E15");var subQ7=sQuery(id+"F0.wireOp",EDGE,"E12.0");Q7=makeQuery(id+"F39.opFillet","BLEND_EDGE",EDGE,{"blendedFrom":[makeQuery(id+"F1.opExtrude","SWEPT_EDGE",EDGE,{"disambiguationData":[OSD([subQ7,subQ6,sQuery(id+"F0.wireOp",EDGE,"E27")])]}),makeQuery(id+"F34.boolean.opBoolean","MERGE",FACE,{"derivedFrom":[makeQuery(id+"F32.boolean.opBoolean","MERGE",FACE,{"derivedFrom":[makeQuery(id+"F31.opBoolean","MERGE",FACE,{"derivedFrom":[makeQuery(id+"F1.opExtrude","CAP_FACE",FACE,{"disambiguationData":[OSD([subQ7,subQ5,sQuery(id+"F0.wireOp",EDGE,"E14"),subQ6,subQ4,subQ3,sQuery(id+"F0.wireOp",EDGE,"E21"),subQ2,sQuery(id+"F0.wireOp",EDGE,"E30")])],"isStart":false}),makeQuery(id+"F2.opExtrude","CAP_FACE",FACE,{"disambiguationData":[OSD([subQ5,subQ4,subQ3,subQ2,subQ1])],"isStart":false})]}),makeQuery(id+"F32.opExtrude","CAP_FACE",FACE,{"disambiguationData":[OSD([subQ0,subQ1])],"isStart":false})]}),makeQuery(id+"F34.opExtrude","CAP_FACE",FACE,{"disambiguationData":[OSD([subQ0,sQuery(id+"F0.wireOp",EDGE,"E1")])],"isStart":false})]})],"blendedInto":[makeQuery(id+"F34.boolean.opBoolean","MERGE",FACE,{"derivedFrom":[makeQuery(id+"F32.boolean.opBoolean","MERGE",FACE,{"derivedFrom":[makeQuery(id+"F31.opBoolean","MERGE",FACE,{"derivedFrom":[makeQuery(id+"F1.opExtrude","CAP_FACE",FACE,{"disambiguationData":[OSD([subQ7,subQ5,sQuery(id+"F0.wireOp",EDGE,"E14"),subQ6,subQ4,subQ3,sQuery(id+"F0.wireOp",EDGE,"E21"),subQ2,sQuery(id+"F0.wireOp",EDGE,"E30")])],"isStart":false}),makeQuery(id+"F2.opExtrude","CAP_FACE",FACE,{"disambiguationData":[OSD([subQ5,subQ4,subQ3,subQ2,subQ1])],"isStart":false})]}),makeQuery(id+"F32.opExtrude","CAP_FACE",FACE,{"disambiguationData":[OSD([subQ0,subQ1])],"isStart":false})]}),makeQuery(id+"F34.opExtrude","CAP_FACE",FACE,{"disambiguationData":[OSD([subQ0,sQuery(id+"F0.wireOp",EDGE,"E1")])],"isStart":false})]})]});}
            fillet(context, id + "F41", {"entities" : qUnion([Q0, Q1, Q2, Q3, Q4, Q5, Q6, Q7]), "radius" : 2 * mm, "tangentPropagation" : true, "allowEdgeOverflow" : false});
        }
        {
            var Q0;
            Q0=makeQuery(id+"F5.opExtrude","SWEPT_EDGE",EDGE,{"disambiguationData":[OSD([sQuery(id+"F0.wireOp",EDGE,"E12.0"),sQuery(id+"F0.wireOp",EDGE,"E15"),sQuery(id+"F0.wireOp",EDGE,"E27"),sQuery(id+"F4.wireOp",EDGE,"E40"),sQuery(id+"F4.wireOp",EDGE,"E42")])]});
            var Q1;
            Q1=makeQuery(id+"F39.opFillet","BLEND_EDGE",EDGE,{"blendedFrom":[makeQuery(id+"F13.boolean.opBoolean","MERGE",EDGE,{"derivedFrom":[makeQuery(id+"F5.opExtrude","CAP_EDGE",EDGE,{"disambiguationData":[OSD([sQuery(id+"F4.wireOp",EDGE,"E40")])],"isStart":false}),makeQuery(id+"F13.opExtrude","SWEPT_EDGE",EDGE,{"disambiguationData":[OSD([sQuery(id+"F0.wireOp",EDGE,"E15"),sQuery(id+"F0.wireOp",EDGE,"E27"),sQuery(id+"F12.wireOp",EDGE,"E49")])]})]}),makeQuery(id+"F5.opExtrude","SWEPT_FACE",FACE,{"disambiguationData":[OSD([sQuery(id+"F4.wireOp",EDGE,"E42")])]})],"blendedInto":[makeQuery(id+"F5.opExtrude","SWEPT_FACE",FACE,{"disambiguationData":[OSD([sQuery(id+"F4.wireOp",EDGE,"E42")])]})]});
            var Q2;
            Q2=makeQuery(id+"F5.opExtrude","SWEPT_EDGE",EDGE,{"disambiguationData":[OSD([sQuery(id+"F0.wireOp",EDGE,"E12.0"),sQuery(id+"F0.wireOp",EDGE,"E21"),sQuery(id+"F0.wireOp",EDGE,"E26"),sQuery(id+"F4.wireOp",EDGE,"E41"),sQuery(id+"F4.wireOp",EDGE,"E42")])]});
            var Q3;
            Q3=makeQuery(id+"F39.opFillet","BLEND_EDGE",EDGE,{"blendedFrom":[makeQuery(id+"F13.boolean.opBoolean","MERGE",EDGE,{"derivedFrom":[makeQuery(id+"F5.opExtrude","CAP_EDGE",EDGE,{"disambiguationData":[OSD([sQuery(id+"F4.wireOp",EDGE,"E41")])],"isStart":false}),makeQuery(id+"F13.opExtrude","SWEPT_EDGE",EDGE,{"disambiguationData":[OSD([sQuery(id+"F0.wireOp",EDGE,"E21"),sQuery(id+"F0.wireOp",EDGE,"E26"),sQuery(id+"F12.wireOp",EDGE,"E50")])]})]}),makeQuery(id+"F5.opExtrude","SWEPT_FACE",FACE,{"disambiguationData":[OSD([sQuery(id+"F4.wireOp",EDGE,"E42")])]})],"blendedInto":[makeQuery(id+"F5.opExtrude","SWEPT_FACE",FACE,{"disambiguationData":[OSD([sQuery(id+"F4.wireOp",EDGE,"E42")])]})]});
            fillet(context, id + "F42", {"entities" : qUnion([Q0, Q1, Q2, Q3]), "radius" : 1.5 * mm, "tangentPropagation" : true, "allowEdgeOverflow" : false});
        }
    });
